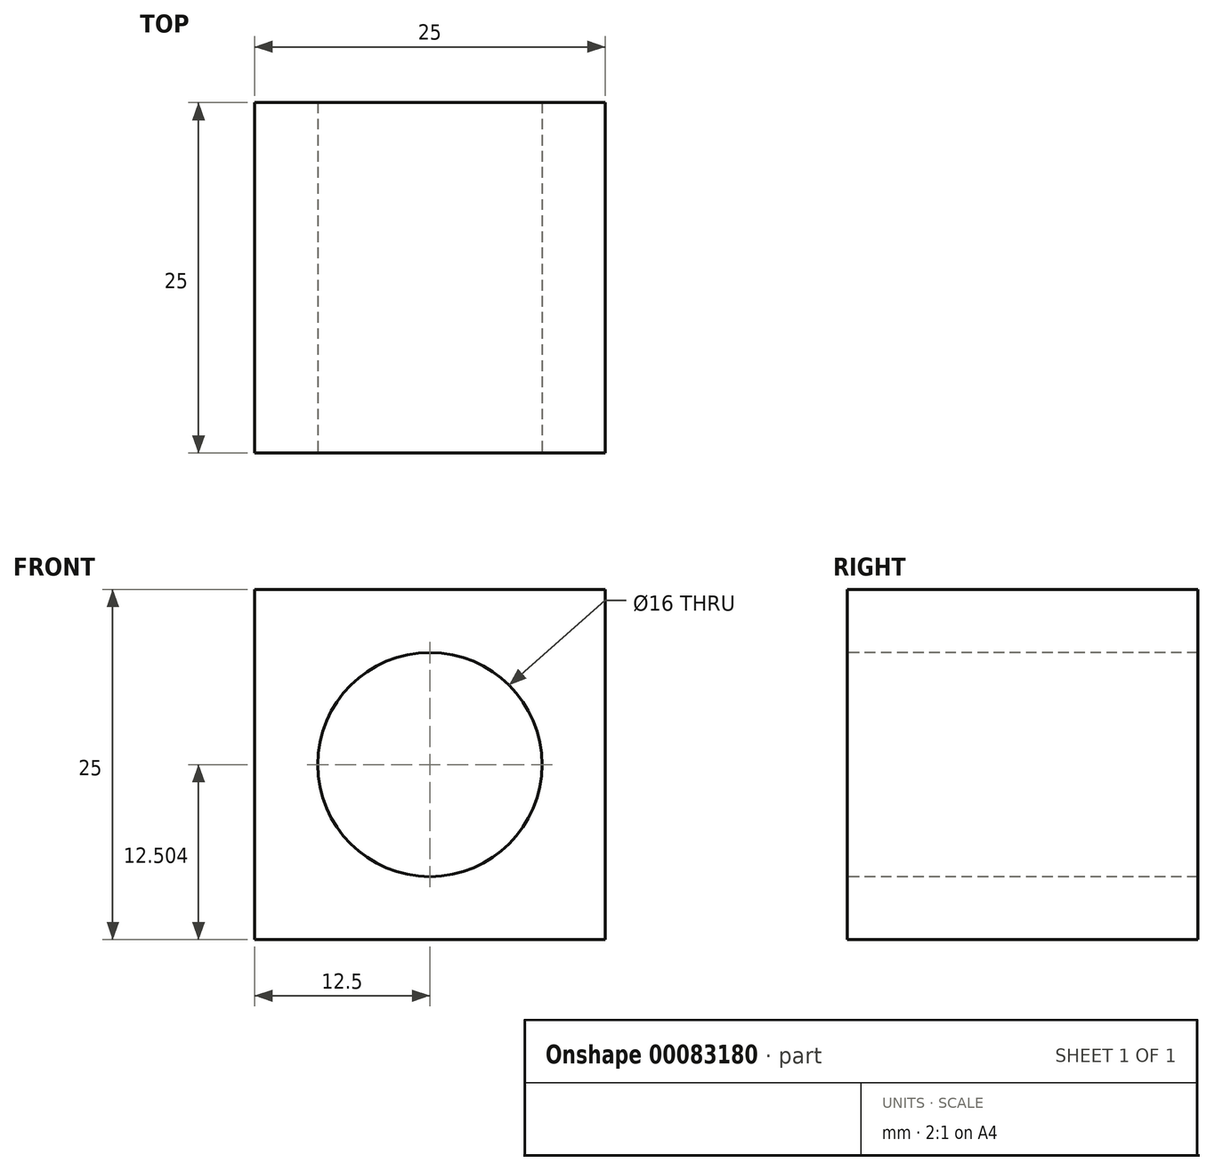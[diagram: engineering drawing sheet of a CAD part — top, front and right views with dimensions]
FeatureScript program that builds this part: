
annotation { "Feature Type Name" : "Feature", "Feature Type Description" : "" }
export const myFeature = defineFeature(function(context is Context, id is Id, definition is map)
    precondition{}
    {
        {
            var Q0;
            Q0=qCreatedBy(makeId("Front.planeOp"),FACE);
            var sketch = newSketch(context, id + "F0", { "sketchPlane" : qUnion([Q0])});
            skLineSegment(sketch, "E0.bottom", {"start": v(-37.33, 16.95) * mm, "end": v(-12.33, 16.95) * mm});
            skLineSegment(sketch, "E0.top", {"start": v(-37.33, -8.05) * mm, "end": v(-12.33, -8.05) * mm});
            skLineSegment(sketch, "E0.left", {"start": v(-37.33, 16.95) * mm, "end": v(-37.33, -8.05) * mm});
            skLineSegment(sketch, "E0.right", {"start": v(-12.33, 16.95) * mm, "end": v(-12.33, -8.05) * mm});
            skSolve(sketch);
        }
        {
            var Q0;
            Q0 = qSketchRegion(id + "F0", true);
            extrude(context, id + "F1", {"entities" : qUnion([Q0]), "depth" : 25 * mm});
        }
        {
            var Q0;
            Q0=makeQuery(id+"F1.opExtrude","CAP_FACE",FACE,{"disambiguationData":[OSD([sQuery(id+"F0.wireOp",EDGE,"E0.bottom"),sQuery(id+"F0.wireOp",EDGE,"E0.top"),sQuery(id+"F0.wireOp",EDGE,"E0.left"),sQuery(id+"F0.wireOp",EDGE,"E0.right")])],"isStart":false});
            var sketch = newSketch(context, id + "F2", { "sketchPlane" : qUnion([Q0])});
            skLineSegment(sketch, "E1", {"start": v(-24.83, 16.95) * mm, "end": v(-24.83, -8.05) * mm});
            skPoint(sketch, "E1.endSnap0", {"position": v(-24.83, -8.05) * mm});
            skLineSegment(sketch, "E2", {"start": v(-12.33, 4.45) * mm, "end": v(-37.33, 4.45) * mm});
            skCircle(sketch, "E3", {"center": v(-24.83, 4.45) * mm, "radius": 8 * mm});
            skSolve(sketch);
        }
        {
            var Q0;
            {var subQ0=sQuery(id+"F2.wireOp",EDGE,"E2");var subQ1=sQuery(id+"F2.wireOp",EDGE,"E1");var subQ2=makeQuery(id+"F2.imprint","INTERSECT",VERTEX,{"derivedFrom":[subQ1,subQ0]});Q0=makeQuery(id+"F2.imprint","IMPRINT",FACE,{"disambiguationData":[TD([[makeQuery(id+"F2.imprint","IMPRINT",EDGE,{"disambiguationData":[TD([[subQ2,-1.0]])],"derivedFrom":subQ1}),-1.0]])]});}
            var Q1;
            {var subQ0=sQuery(id+"F2.wireOp",EDGE,"E3");var subQ1=sQuery(id+"F2.wireOp",EDGE,"E1");var subQ2=makeQuery(id+"F2.imprint","INTERSECT",VERTEX,{"disambiguationData":[OD(0.0)],"derivedFrom":[subQ1,subQ0]});Q1=makeQuery(id+"F2.imprint","IMPRINT",FACE,{"disambiguationData":[TD([[makeQuery(id+"F2.imprint","IMPRINT",EDGE,{"disambiguationData":[TD([[subQ2,-1.0]])],"derivedFrom":subQ1}),-1.0]])]});}
            var Q2;
            {var subQ0=sQuery(id+"F2.wireOp",EDGE,"E3");var subQ1=sQuery(id+"F2.wireOp",EDGE,"E1");var subQ2=makeQuery(id+"F2.imprint","INTERSECT",VERTEX,{"disambiguationData":[OD(0.0)],"derivedFrom":[subQ1,subQ0]});Q2=makeQuery(id+"F2.imprint","IMPRINT",FACE,{"disambiguationData":[TD([[makeQuery(id+"F2.imprint","IMPRINT",EDGE,{"disambiguationData":[TD([[subQ2,-1.0]])],"derivedFrom":subQ1}),1.0]])]});}
            var Q3;
            {var subQ0=sQuery(id+"F2.wireOp",EDGE,"E2");var subQ1=sQuery(id+"F2.wireOp",EDGE,"E1");var subQ2=makeQuery(id+"F2.imprint","INTERSECT",VERTEX,{"derivedFrom":[subQ1,subQ0]});Q3=makeQuery(id+"F2.imprint","IMPRINT",FACE,{"disambiguationData":[TD([[makeQuery(id+"F2.imprint","IMPRINT",EDGE,{"disambiguationData":[TD([[subQ2,-1.0]])],"derivedFrom":subQ1}),1.0]])]});}
            extrude(context, id + "F3", {"entities" : qUnion([Q0, Q1, Q2, Q3]), "operationType" : NewBodyOperationType.REMOVE, "oppositeDirection" : true, "depth" : 25 * mm});
        }
    });
